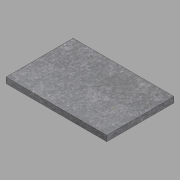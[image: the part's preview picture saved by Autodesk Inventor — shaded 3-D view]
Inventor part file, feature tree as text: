
AUTODESK INVENTOR PART (.ipt)
format: ipt  version: 2022.2 (Build 262287000, 287)  size: 115,200 bytes
history: native  units: in
note: dims shown in document units (in); Inventor stores cm internally (conversion verified against a paired STEP export)
features: extrude x1, sketch x1
ambient origin geometry x8: Origin, YZ Plane, XZ Plane, XY Plane, X Axis, Y Axis, Z Axis, Center Point
bodies: Body1 (feature_tree)
feature tree (2):
  extrude  "Extrusion2"  Depth=24.0in
  sketch  "Sketch3"  dims[d4=36.0in d5=24.0in d6=2.0in d7=0.0in]
